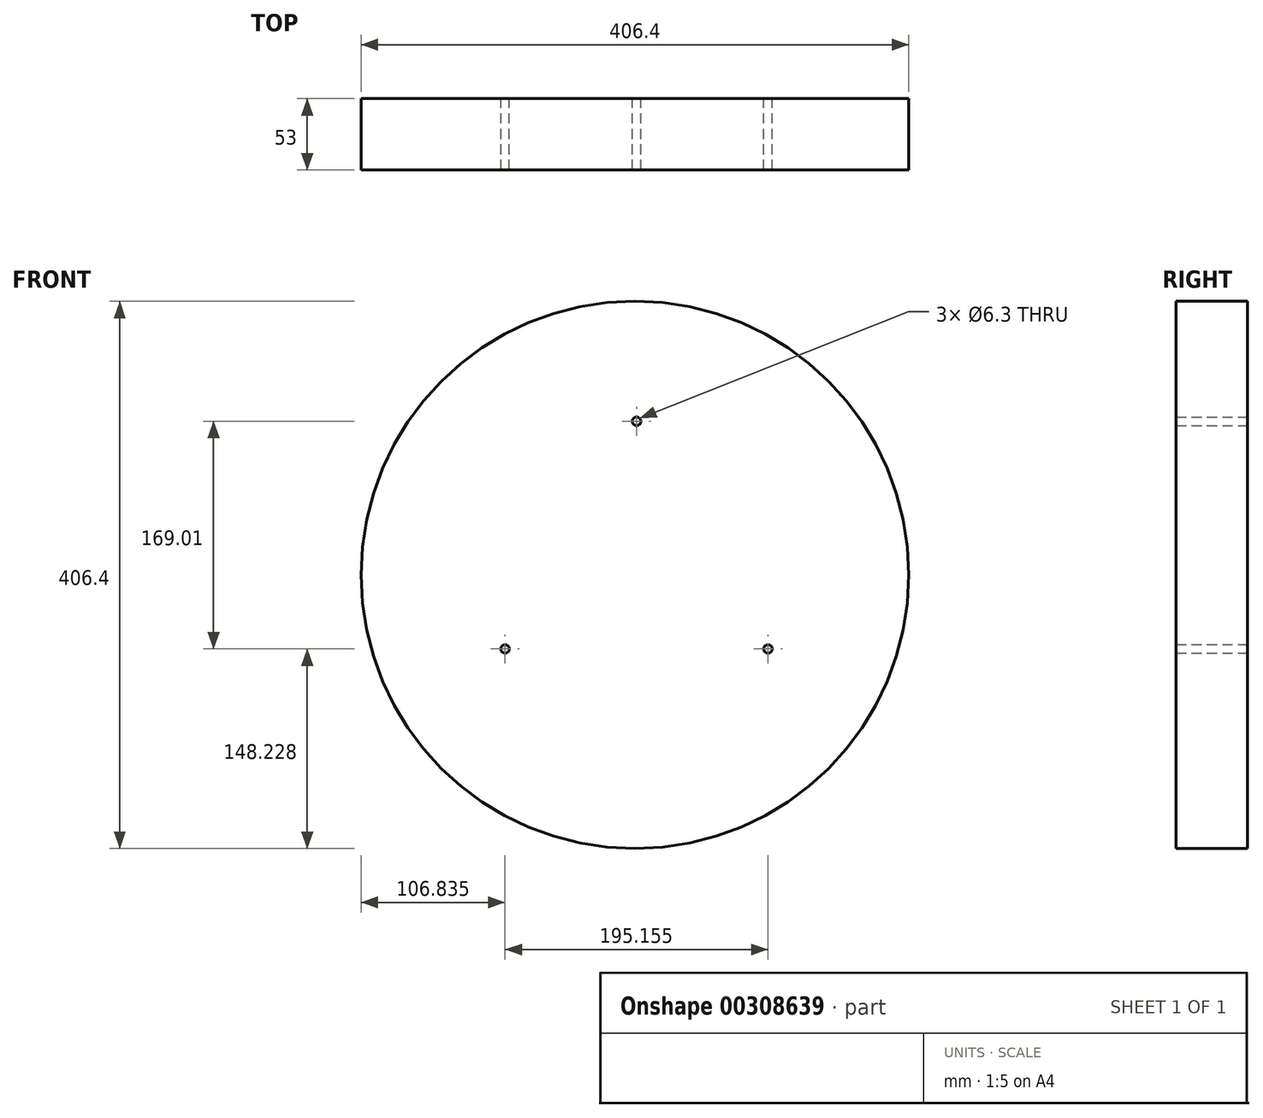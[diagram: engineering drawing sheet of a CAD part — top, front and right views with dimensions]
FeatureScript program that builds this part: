
annotation { "Feature Type Name" : "Feature", "Feature Type Description" : "" }
export const myFeature = defineFeature(function(context is Context, id is Id, definition is map)
    precondition{}
    {
        {
            var Q0;
            Q0=qCreatedBy(makeId("Front.planeOp"),FACE);
            var sketch = newSketch(context, id + "F0", { "sketchPlane" : qUnion([Q0])});
            skCircle(sketch, "E0", {"center": v(0, 0) * mm, "radius": 203.2 * mm});
            skCircle(sketch, "E1", {"center": v(0, 0) * mm, "radius": 161.76 * mm, "construction": true});
            skCircle(sketch, "E2", {"center": v(0, 0) * mm, "radius": 77.88 * mm, "construction": true});
            skCircle(sketch, "E3", {"center": v(1.21, 1.36) * mm, "radius": 77.88 * mm, "construction": true});
            skCircle(sketch, "E4.0", {"center": v(1.21, 1.36) * mm, "radius": 87.88 * mm, "construction": true});
            skCircle(sketch, "E5.0", {"center": v(1.21, 1.36) * mm, "radius": 67.88 * mm, "construction": true});
            skCircle(sketch, "E6", {"center": v(1.21, 1.36) * mm, "radius": 112.67 * mm, "construction": true});
            skCircle(sketch, "E7", {"center": v(1.21, 114.04) * mm, "radius": 3.15 * mm});
            skCircle(sketch, "E8.1.0", {"center": v(-96.36, -54.97) * mm, "radius": 3.15 * mm});
            skCircle(sketch, "E8.2.0", {"center": v(98.8, -54.97) * mm, "radius": 3.15 * mm});
            skSolve(sketch);
        }
        {
            var Q0;
            Q0=qSketchRegion(id+"F0",true);
            extrude(context, id + "F1", {"entities" : qUnion([Q0]), "depth" : 53 * mm});
        }
    });
